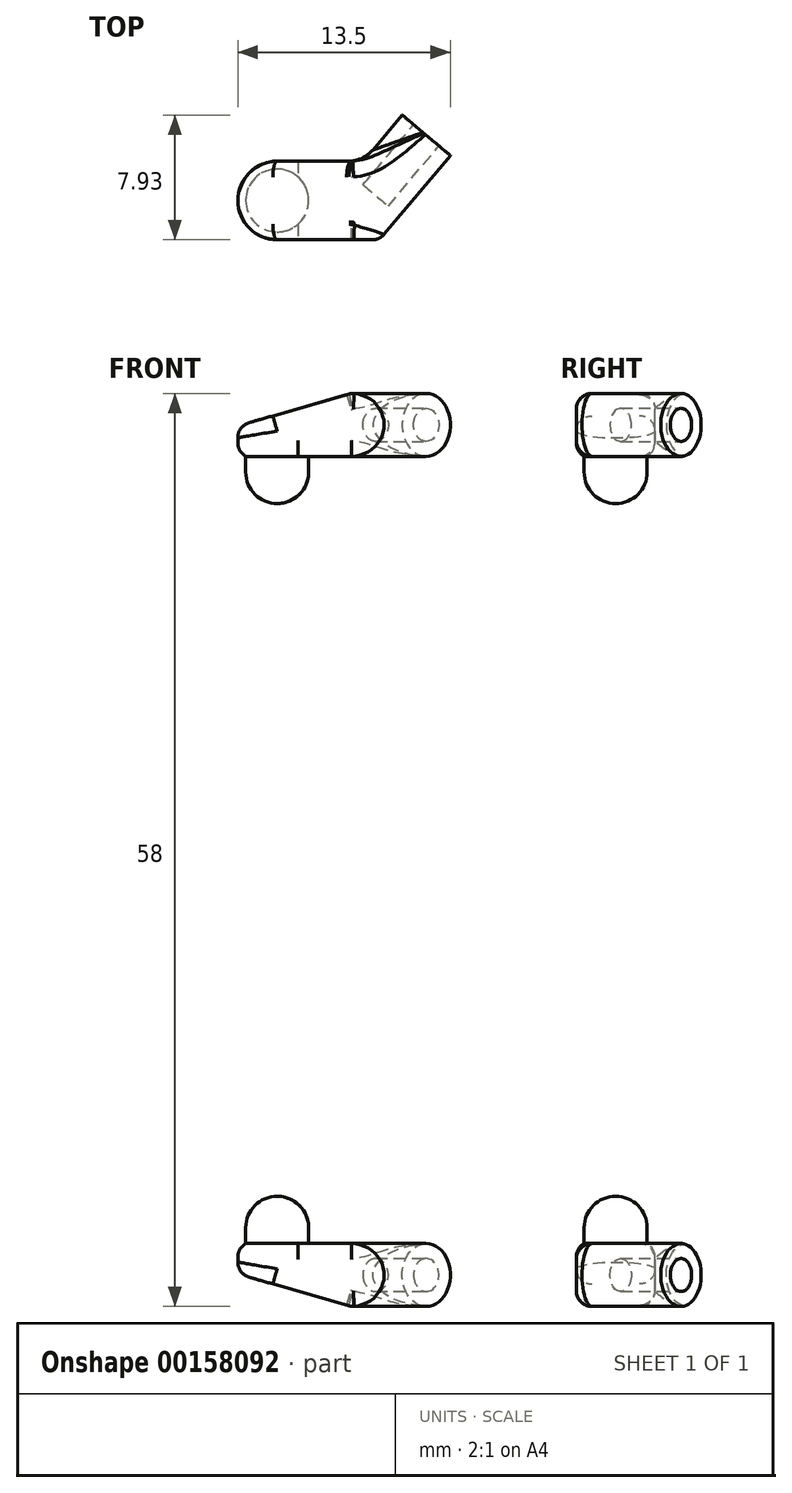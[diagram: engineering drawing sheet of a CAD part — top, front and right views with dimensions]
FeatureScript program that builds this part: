
annotation { "Feature Type Name" : "Feature", "Feature Type Description" : "" }
export const myFeature = defineFeature(function(context is Context, id is Id, definition is map)
    precondition{}
    {
        {
            var Q0;
            Q0=qCreatedBy(makeId("Top.planeOp"),FACE);
            var sketch = newSketch(context, id + "F0", { "sketchPlane" : qUnion([Q0])});
            skCircle(sketch, "E0", {"center": v(0, 0) * mm, "radius": 2 * mm});
            skSolve(sketch);
        }
        {
            var Q0;
            Q0=makeQuery(id+"F0.imprint","IMPRINT",FACE,{"disambiguationData":[TD([[makeQuery(id+"F0.imprint","IMPRINT",EDGE,{"derivedFrom":sQuery(id+"F0.wireOp",EDGE,"E0")}),1.0]])]});
            extrude(context, id + "F1", {"entities" : qUnion([Q0]), "depth" : 3 * mm});
        }
        {
            var Q0;
            Q0=makeQuery(id+"F1.opExtrude","CAP_FACE",FACE,{"disambiguationData":[OSD([sQuery(id+"F0.wireOp",EDGE,"E0")])],"isStart":false});
            var sketch = newSketch(context, id + "F2", { "sketchPlane" : qUnion([Q0])});
            skArc(sketch, "E1", {"start": v(0, 2.5) * mm, "mid": v(-2.5, 0) * mm, "end": v(0, -2.5) * mm});
            skLineSegment(sketch, "E2", {"start": v(0, 2.5) * mm, "end": v(5.47, 2.5) * mm});
            skLineSegment(sketch, "E3", {"start": v(0, -2.5) * mm, "end": v(6.5, -2.5) * mm});
            skLineSegment(sketch, "E4", {"start": v(6.5, -2.5) * mm, "end": v(11, 2.86) * mm});
            skLineSegment(sketch, "E5", {"start": v(11, 2.86) * mm, "end": v(7.94, 5.43) * mm});
            skLineSegment(sketch, "E6", {"start": v(7.94, 5.43) * mm, "end": v(5.47, 2.5) * mm});
            skSolve(sketch);
        }
        {
            var Q0;
            Q0=makeQuery(id+"F2.imprint","IMPRINT",FACE,{"disambiguationData":[TD([[makeQuery(id+"F2.imprint","IMPRINT",EDGE,{"derivedFrom":sQuery(id+"F2.wireOp",EDGE,"E1")}),1.0]])]});
            var Q1;
            Q1=makeQuery(id+"F2.imprint","IMPRINT",FACE,{"disambiguationData":[TD([[makeQuery(id+"F2.imprint","IMPRINT",EDGE,{"derivedFrom":makeQuery(id+"F1.opExtrude","CAP_EDGE",EDGE,{"disambiguationData":[OSD([sQuery(id+"F0.wireOp",EDGE,"E0")])],"isStart":false})}),1.0]])]});
            extrude(context, id + "F3", {"entities" : qUnion([Q0, Q1]), "operationType" : NewBodyOperationType.ADD, "depth" : 4 * mm});
        }
        {
            var Q0;
            Q0=makeQuery(id+"F3.opExtrude","CAP_EDGE",EDGE,{"disambiguationData":[OSD([sQuery(id+"F2.wireOp",EDGE,"E4")])],"isStart":false});
            var Q1;
            Q1=makeQuery(id+"F3.opExtrude","CAP_EDGE",EDGE,{"disambiguationData":[OSD([sQuery(id+"F2.wireOp",EDGE,"E6")])],"isStart":false});
            var Q2;
            Q2=makeQuery(id+"F3.opExtrude","CAP_EDGE",EDGE,{"disambiguationData":[OSD([sQuery(id+"F2.wireOp",EDGE,"E4")])],"isStart":true});
            var Q3;
            Q3=makeQuery(id+"F3.opExtrude","CAP_EDGE",EDGE,{"disambiguationData":[OSD([sQuery(id+"F2.wireOp",EDGE,"E6")])],"isStart":true});
            fillet(context, id + "F4", {"entities" : qUnion([Q0, Q1, Q2, Q3]), "radius" : 2 * mm, "tangentPropagation" : true, "allowEdgeOverflow" : false});
        }
        {
            var Q0;
            Q0=makeQuery(id+"F4.opFillet","BLEND_EDGE",EDGE,{"blendedFrom":[makeQuery(id+"F3.opExtrude","CAP_EDGE",EDGE,{"disambiguationData":[OSD([sQuery(id+"F2.wireOp",EDGE,"E6")])],"isStart":true}),makeQuery(id+"F3.opExtrude","SWEPT_FACE",FACE,{"disambiguationData":[OSD([sQuery(id+"F2.wireOp",EDGE,"E2")])]})],"blendedInto":[makeQuery(id+"F3.opExtrude","SWEPT_FACE",FACE,{"disambiguationData":[OSD([sQuery(id+"F2.wireOp",EDGE,"E2")])]})]});
            fillet(context, id + "F5", {"entities" : qUnion([Q0]), "radius" : 2 * mm, "tangentPropagation" : true, "allowEdgeOverflow" : false});
        }
        {
            var Q0;
            Q0=makeQuery(id+"F3.opExtrude","CAP_EDGE",EDGE,{"disambiguationData":[OSD([sQuery(id+"F2.wireOp",EDGE,"E3")])],"isStart":false});
            var Q1;
            Q1=makeQuery(id+"F3.opExtrude","CAP_EDGE",EDGE,{"disambiguationData":[OSD([sQuery(id+"F2.wireOp",EDGE,"E1")])],"isStart":false});
            fillet(context, id + "F6", {"entities" : qUnion([Q0, Q1]), "radius" : 1 * mm, "tangentPropagation" : true, "allowEdgeOverflow" : false});
        }
        {
            var Q0;
            Q0=makeQuery(id+"F1.opExtrude","CAP_EDGE",EDGE,{"disambiguationData":[OSD([sQuery(id+"F0.wireOp",EDGE,"E0")])],"isStart":true});
            fillet(context, id + "F7", {"entities" : qUnion([Q0]), "radius" : 2 * mm, "tangentPropagation" : true, "allowEdgeOverflow" : false});
        }
        {
            var Q0;
            Q0=makeQuery(id+"F3.opExtrude","SWEPT_FACE",FACE,{"disambiguationData":[OSD([sQuery(id+"F2.wireOp",EDGE,"E5")])]});
            var sketch = newSketch(context, id + "F8", { "sketchPlane" : qUnion([Q0])});
            skCircle(sketch, "E7", {"center": v(-4.59, 5) * mm, "radius": 1.05 * mm});
            skSolve(sketch);
        }
        {
            var Q0;
            Q0=makeQuery(id+"F8.imprint","IMPRINT",FACE,{"disambiguationData":[TD([[makeQuery(id+"F8.imprint","IMPRINT",EDGE,{"derivedFrom":sQuery(id+"F8.wireOp",EDGE,"E7")}),1.0]])]});
            extrude(context, id + "F9", {"entities" : qUnion([Q0]), "operationType" : NewBodyOperationType.REMOVE, "oppositeDirection" : true, "depth" : 5 * mm});
        }
        {
            var Q0;
            Q0=makeQuery(id+"F3.opExtrude","SWEPT_FACE",FACE,{"disambiguationData":[OSD([sQuery(id+"F2.wireOp",EDGE,"E2")])]});
            var sketch = newSketch(context, id + "F10", { "sketchPlane" : qUnion([Q0])});
            skPoint(sketch, "E8.0", {"position": v(-4.7, 7) * mm});
            skLineSegment(sketch, "E9", {"start": v(2.5, 6) * mm, "end": v(2.5, 3.87) * mm});
            skLineSegment(sketch, "E10", {"start": v(2.5, 4.93) * mm, "end": v(-4.7, 7) * mm});
            skLineSegment(sketch, "E11", {"start": v(-4.7, 7) * mm, "end": v(3.86, 7) * mm});
            skLineSegment(sketch, "E12", {"start": v(2.5, 4.93) * mm, "end": v(3.86, 7) * mm});
            skSolve(sketch);
        }
        {
            var Q0;
            {var subQ1=sQuery(id+"F10.wireOp",EDGE,"E11");Q0=makeQuery(id+"F10.imprint","IMPRINT",FACE,{"disambiguationData":[TD([[makeQuery(id+"F10.imprint","IMPRINT",EDGE,{"derivedFrom":subQ1}),-1.0]])]});}
            var Q1;
            {var subQ0=sQuery(id+"F10.wireOp",EDGE,"E10");var subQ1=sQuery(id+"F2.wireOp",EDGE,"E2");var subQ2=makeQuery(id+"F3.opExtrude","SWEPT_EDGE",EDGE,{"disambiguationData":[OSD([sQuery(id+"F2.wireOp",EDGE,"E1"),subQ1])]});var subQ3=makeQuery(id+"F10.imprint","INTERSECT",VERTEX,{"derivedFrom":[subQ2,subQ0]});Q1=makeQuery(id+"F10.imprint","IMPRINT",FACE,{"disambiguationData":[TD([[makeQuery(id+"F10.imprint","IMPRINT",EDGE,{"disambiguationData":[TD([[subQ3,-1.0]])],"derivedFrom":subQ0}),-1.0]])]});}
            extrude(context, id + "F11", {"entities" : qUnion([Q0, Q1]), "operationType" : NewBodyOperationType.REMOVE, "oppositeDirection" : true, "depth" : 25 * mm});
        }
        {
            var Q0;
            {var subQ0=sQuery(id+"F2.wireOp",EDGE,"E2");Q0=makeQuery(id+"F11.boolean.opBoolean","INTERSECT",EDGE,{"derivedFrom":[makeQuery(id+"F6.opFillet","BLEND_FACE",FACE,{"disambiguationData":[OSD([subQ0]),TDD([makeQuery(id+"F3.opExtrude","CAP_EDGE",EDGE,{"disambiguationData":[OSD([subQ0])],"isStart":false})])]}),makeQuery(id+"F11.opExtrude","SWEPT_FACE",FACE,{"disambiguationData":[OSD([sQuery(id+"F10.wireOp",EDGE,"E10")])]})]});}
            fillet(context, id + "F12", {"entities" : qUnion([Q0]), "radius" : 1 * mm, "tangentPropagation" : true, "allowEdgeOverflow" : false});
        }
        {
            var Q0;
            Q0=makeQuery(id+"F3.opExtrude","CAP_FACE",FACE,{"disambiguationData":[OSD([sQuery(id+"F2.wireOp",EDGE,"E1"),sQuery(id+"F2.wireOp",EDGE,"E2"),sQuery(id+"F2.wireOp",EDGE,"E3"),sQuery(id+"F2.wireOp",EDGE,"E4"),sQuery(id+"F2.wireOp",EDGE,"E5"),sQuery(id+"F2.wireOp",EDGE,"E6")])],"isStart":true});
            cPlane(context, id + "F13", {"entities" : qUnion([Q0]), "cplaneType" : CPlaneType.OFFSET, "offset" : 25 * mm, "width" : 150 * mm, "height" : 150 * mm});
        }
        {
            var Q0;
            Q0=makeQuery(id+"F1.opExtrude","SWEPT_BODY",BODY,{"disambiguationData":[OSD([sQuery(id+"F0.wireOp",EDGE,"E0")])]});
            var Q1;
            Q1=qCreatedBy(id+"F13.planeOp",FACE);
            mirror(context, id + "F14", {"entities" : qUnion([Q0]), "mirrorPlane" : qUnion([Q1])});
        }
    });
